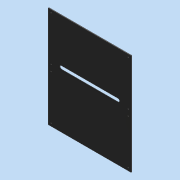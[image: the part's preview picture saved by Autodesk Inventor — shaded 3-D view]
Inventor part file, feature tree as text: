
AUTODESK INVENTOR PART (.ipt)
format: ipt  version: 2016 (Build 200138000, 138)  size: 113,664 bytes
history: native  units: mm
features: hole x8, extrude x2, sketch x2, fillet x1
ambient origin geometry x8: Origin, YZ Plane, XZ Plane, XY Plane, X Axis, Y Axis, Z Axis, Center Point
bodies: Solid1 (feature_tree)
feature tree (13):
  extrude  "Extrusion1"  Depth=440.0mm
  hole  "Hole1"  [1 undecoded]
  hole  "Hole2"  [1 undecoded]
  hole  "Hole3"  [1 undecoded]
  hole  "Hole4"  [1 undecoded]
  hole  "Hole5"  [1 undecoded]
  hole  "Hole6"  [1 undecoded]
  hole  "Hole7"  [1 undecoded]
  hole  "Hole8"  [1 undecoded]
  extrude  "Extrusion2"  Depth=3.0mm TaperAngle=0.0deg
  fillet  "Fillet1"  Radius=2.0mm
  sketch  "Sketch1"  dims[d0=360.0mm d1=440.0mm]
  sketch  "Sketch2"  dims[d2=3.0mm d3=0.0mm d4=12.0mm d5=12.0mm d6=4.0mm d7=6.0mm d8=4.0mm d9=2.0mm d10=90.0deg d11=8.0mm d12=20.594885mm d13=12.0mm d14=12.0mm d15=4.0mm d16=6.0mm d17=4.0mm d18=2.0mm d19=90.0deg d20=8.0mm d21=20.594885mm d22=12.0mm d23=12.0mm d24=4.0mm d25=6.0mm d26=4.0mm d27=2.0mm d28=90.0deg d29=8.0mm d30=20.594885mm d31=12.0mm d32=12.0mm d33=4.0mm d34=6.0mm d35=4.0mm d36=2.0mm d37=90.0deg d38=8.0mm d39=20.594885mm d40=12.0mm d41=206.5mm d42=4.0mm d43=6.0mm d44=4.0mm d45=2.0mm d46=90.0deg d47=8.0mm d48=20.594885mm d49=12.0mm d50=206.5mm d51=4.0mm d52=6.0mm d53=4.0mm d54=2.0mm d55=90.0deg d56=8.0mm d57=20.594885mm d58=12.0mm d59=206.5mm d60=4.0mm d61=6.0mm d62=4.0mm d63=2.0mm d64=90.0deg d65=8.0mm d66=20.594885mm d67=12.0mm d68=206.5mm d69=4.0mm d70=6.0mm d71=4.0mm d72=2.0mm d73=90.0deg d74=8.0mm d75=20.594885mm d76=3.0mm d77=0.0mm d78=2.0mm]
note: 8 required parameter values undecoded (feature->parameter linkage not recoverable at this tier; creation-order binding heuristic only, values carry confidence <= 0.55)
